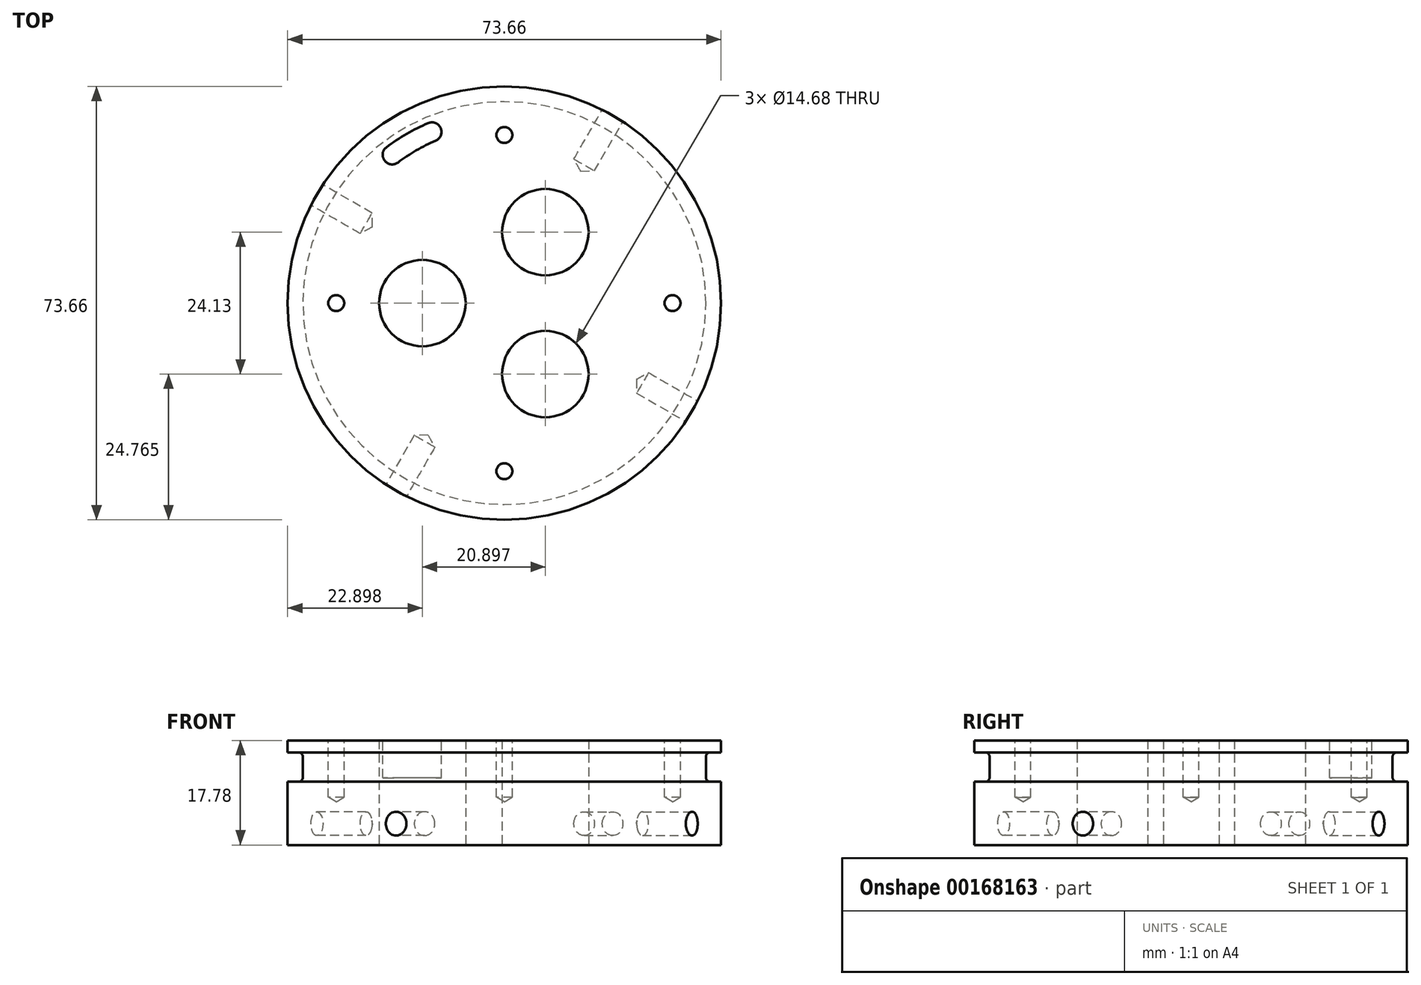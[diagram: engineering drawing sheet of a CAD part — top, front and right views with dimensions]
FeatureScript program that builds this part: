
annotation { "Feature Type Name" : "Feature", "Feature Type Description" : "" }
export const myFeature = defineFeature(function(context is Context, id is Id, definition is map)
    precondition{}
    {
        {
            var Q0;
            Q0=qCreatedBy(makeId("Top.planeOp"),FACE);
            var sketch = newSketch(context, id + "F0", { "sketchPlane" : qUnion([Q0])});
            skCircle(sketch, "E0", {"center": v(0, 0) * mm, "radius": 36.83 * mm});
            skSolve(sketch);
        }
        {
            var Q0;
            Q0=makeQuery(id+"F0.imprint","IMPRINT",FACE,{"disambiguationData":[TD([[makeQuery(id+"F0.imprint","IMPRINT",EDGE,{"derivedFrom":sQuery(id+"F0.wireOp",EDGE,"E0")}),1.0]])]});
            extrude(context, id + "F1", {"entities" : qUnion([Q0]), "depth" : 17.78 * mm});
        }
        {
            var Q0;
            {var subQ0=makeQuery(id+"FhJubWmbG7UBd7M_1.boolean.opBoolean","COPY",FACE,{"derivedFrom":makeQuery(id+"FhJubWmbG7UBd7M_1.opExtrude","SWEPT_FACE",FACE,{"disambiguationData":[OSD([sQuery(id+"FRuIeaWD6VeLny9_1.wireOp",EDGE,"idePJaX5-tPPE-BKw2-N1m4-zZUQrY6AHjir")])]})});Q0=makeQuery(id+"FOQC5dfjhO448EJ_1.boolean.opBoolean","SPLIT",FACE,{"disambiguationData":[TD([subQ0])],"derivedFrom":makeQuery(id+"FkcieFRIapZdHPD_1.boolean.opBoolean","SPLIT",FACE,{"disambiguationData":[TD([subQ0])],"derivedFrom":makeQuery(id+"F1.opExtrude","CAP_FACE",FACE,{"disambiguationData":[OSD([sQuery(id+"F0.wireOp",EDGE,"E0")])],"isStart":false})})});}
            var sketch = newSketch(context, id + "F2", { "sketchPlane" : qUnion([Q0])});
            skCircle(sketch, "E1", {"center": v(0, 0) * mm, "radius": 28.58 * mm, "construction": true});
            skLineSegment(sketch, "E2", {"start": v(0, 0) * mm, "end": v(28.57, 0) * mm, "construction": true});
            skPoint(sketch, "E3", {"position": v(28.58, 0) * mm});
            skPoint(sketch, "E4.1.0", {"position": v(0, 28.58) * mm});
            skPoint(sketch, "E4.2.0", {"position": v(-28.58, 0) * mm});
            skPoint(sketch, "E4.3.0", {"position": v(0, -28.58) * mm});
            skSolve(sketch);
        }
        {
            var Q0;
            Q0=sQuery(id+"F2.wireOp",VERTEX,"E3");
            var Q1;
            Q1=sQuery(id+"F2.wireOp",VERTEX,"E4.3.0");
            var Q2;
            Q2=sQuery(id+"F2.wireOp",VERTEX,"E4.2.0");
            var Q3;
            Q3=sQuery(id+"F2.wireOp",VERTEX,"E4.1.0");
            var Q4;
            Q4=makeQuery(id+"F1.opExtrude","SWEPT_BODY",BODY,{"disambiguationData":[OSD([sQuery(id+"F0.wireOp",EDGE,"E0")])]});
            hole(context, id + "F3", {"style" : HoleStyle.SIMPLE, "endStyle" : HoleEndStyle.BLIND, "standardTappedOrClearance" : lookupTablePath({ "standard" : "ANSI", "engagement" : "75%", "pitch" : "32 tpi", "size" : "#6", "type" : "Tapped" }), "standardBlindInLast" : lookupTablePath({ "standard" : "ANSI", "engagement" : "75%", "pitch" : "32 tpi", "size" : "#6", "type" : "Tapped" }), "holeDiameter" : 2.7 * mm, "holeDepth" : 9.65 * mm, "locations" : qUnion([Q0, Q1, Q2, Q3]), "scope" : qUnion([Q4]), "majorDiameter" : 3.5 * mm});
        }
        {
            var Q0;
            Q0=makeQuery(id+"FOQC5dfjhO448EJ_1.boolean.opBoolean","SPLIT",FACE,{"disambiguationData":[TD([makeQuery(id+"FhJubWmbG7UBd7M_1.boolean.opBoolean","COPY",FACE,{"derivedFrom":makeQuery(id+"FhJubWmbG7UBd7M_1.opExtrude","SWEPT_FACE",FACE,{"disambiguationData":[OSD([sQuery(id+"FRuIeaWD6VeLny9_1.wireOp",EDGE,"idePJaX5-tPPE-BKw2-N1m4-zZUQrY6AHjir")])]})})])],"derivedFrom":makeQuery(id+"F1.opExtrude","CAP_FACE",FACE,{"disambiguationData":[OSD([sQuery(id+"F0.wireOp",EDGE,"E0")])],"isStart":false})});
            cPlane(context, id + "F4", {"entities" : qUnion([Q0]), "cplaneType" : CPlaneType.OFFSET, "offset" : 2.03 * mm, "oppositeDirection" : true, "width" : 152.4 * mm, "height" : 152.4 * mm});
        }
        {
            var Q0;
            Q0=qCreatedBy(id+"F4.planeOp",FACE);
            var sketch = newSketch(context, id + "F5", { "sketchPlane" : qUnion([Q0])});
            skCircle(sketch, "E5", {"center": v(0, 0) * mm, "radius": 34.24 * mm});
            skCircle(sketch, "E6.0", {"center": v(0, 0) * mm, "radius": 36.83 * mm});
            skSolve(sketch);
        }
        {
            var Q0;
            Q0=qSketchRegion(id+"F5",true);
            extrude(context, id + "F6", {"entities" : qUnion([Q0]), "operationType" : NewBodyOperationType.REMOVE, "oppositeDirection" : true, "depth" : 5 * mm});
        }
        {
            var Q0;
            Q0=makeQuery(id+"F6.boolean.opBoolean","COPY",EDGE,{"derivedFrom":makeQuery(id+"F6.opExtrude","CAP_EDGE",EDGE,{"disambiguationData":[OSD([sQuery(id+"F5.wireOp",EDGE,"E5")])],"isStart":false})});
            var Q1;
            Q1=makeQuery(id+"F6.boolean.opBoolean","COPY",EDGE,{"derivedFrom":makeQuery(id+"F6.opExtrude","CAP_EDGE",EDGE,{"disambiguationData":[OSD([sQuery(id+"F5.wireOp",EDGE,"E5")])],"isStart":true})});
            fillet(context, id + "F7", {"entities" : qUnion([Q0, Q1]), "radius" : 0.76 * mm, "tangentPropagation" : true, "allowEdgeOverflow" : false});
        }
        {
            var Q0;
            {var subQ1=sQuery(id+"F0.wireOp",EDGE,"E0");var subQ2=makeQuery(id+"F1.opExtrude","SWEPT_FACE",FACE,{"disambiguationData":[OSD([subQ1])]});Q0=makeQuery(id+"FkcieFRIapZdHPD_1.boolean.opBoolean","SPLIT",FACE,{"disambiguationData":[TD([subQ2])],"derivedFrom":makeQuery(id+"F1.opExtrude","CAP_FACE",FACE,{"disambiguationData":[OSD([subQ1])],"isStart":false})});}
            var sketch = newSketch(context, id + "F8", { "sketchPlane" : qUnion([Q0])});
            skCircle(sketch, "E7.0", {"center": v(0, 0) * mm, "radius": 36.83 * mm, "construction": true});
            skPoint(sketch, "E8", {"position": v(-18.41, -31.9) * mm});
            skLineSegment(sketch, "E9", {"start": v(0, -36.83) * mm, "end": v(0, 0) * mm, "construction": true});
            skLineSegment(sketch, "E10", {"start": v(0, 0) * mm, "end": v(-17.96, -31.1) * mm, "construction": true});
            skLineSegment(sketch, "E11", {"start": v(-17.96, -31.1) * mm, "end": v(-18.41, -31.9) * mm, "construction": true});
            skLineSegment(sketch, "E12", {"start": v(0, 0) * mm, "end": v(18.41, 31.9) * mm, "construction": true});
            skLineSegment(sketch, "E13", {"start": v(18.41, 31.9) * mm, "end": v(0, 0) * mm, "construction": true});
            skLineSegment(sketch, "E14", {"start": v(31.9, -18.41) * mm, "end": v(0, 0) * mm, "construction": true});
            skLineSegment(sketch, "E15", {"start": v(0, 0) * mm, "end": v(-31.9, 18.41) * mm, "construction": true});
            skPoint(sketch, "E16", {"position": v(18.41, 31.9) * mm});
            skPoint(sketch, "E17", {"position": v(31.9, -18.41) * mm});
            skPoint(sketch, "E18", {"position": v(-31.9, 18.41) * mm});
            skSolve(sketch);
        }
        {
            var Q0;
            Q0=qCreatedBy(makeId("Front.planeOp"),FACE);
            var sketch = newSketch(context, id + "F9", { "sketchPlane" : qUnion([Q0])});
            skLineSegment(sketch, "E19", {"start": v(0, 0) * mm, "end": v(0, 38.57) * mm, "construction": true});
            skSolve(sketch);
        }
        {
            var Q0;
            Q0=sQuery(id+"F9.wireOp",EDGE,"E19");
            cPlane(context, id + "F10", {"entities" : qUnion([Q0]), "cplaneType" : CPlaneType.LINE_ANGLE, "offset" : 25.4 * mm, "angle" : 60 * degree, "width" : 152.4 * mm, "height" : 152.4 * mm});
        }
        {
            var Q0;
            Q0=sQuery(id+"F8.wireOp",VERTEX,"E8");
            var Q1;
            Q1=qCreatedBy(id+"F10.planeOp",FACE);
            cPlane(context, id + "F11", {"entities" : qUnion([Q0, Q1]), "cplaneType" : CPlaneType.PLANE_POINT, "offset" : 25.4 * mm, "width" : 152.4 * mm, "height" : 152.4 * mm});
        }
        {
            var Q0;
            Q0=qCreatedBy(id+"F11.planeOp",FACE);
            var Q1;
            Q1=sQuery(id+"F8.wireOp",VERTEX,"E16");
            cPlane(context, id + "F12", {"entities" : qUnion([Q0, Q1]), "cplaneType" : CPlaneType.PLANE_POINT, "offset" : 25.4 * mm, "width" : 152.4 * mm, "height" : 152.4 * mm});
        }
        {
            var Q0;
            Q0=sQuery(id+"F9.wireOp",EDGE,"E19");
            cPlane(context, id + "F13", {"entities" : qUnion([Q0]), "cplaneType" : CPlaneType.LINE_ANGLE, "offset" : 25.4 * mm, "angle" : 150 * degree, "width" : 152.4 * mm, "height" : 152.4 * mm});
        }
        {
            var Q0;
            Q0=sQuery(id+"F8.wireOp",VERTEX,"E18");
            var Q1;
            Q1=qCreatedBy(id+"F13.planeOp",FACE);
            cPlane(context, id + "F14", {"entities" : qUnion([Q0, Q1]), "cplaneType" : CPlaneType.PLANE_POINT, "offset" : 25.4 * mm, "width" : 152.4 * mm, "height" : 152.4 * mm});
        }
        {
            var Q0;
            Q0=qCreatedBy(id+"F13.planeOp",FACE);
            var Q1;
            Q1=sQuery(id+"F8.wireOp",VERTEX,"E17");
            cPlane(context, id + "F15", {"entities" : qUnion([Q0, Q1]), "cplaneType" : CPlaneType.PLANE_POINT, "offset" : 25.4 * mm, "width" : 152.4 * mm, "height" : 152.4 * mm});
        }
        {
            var Q0;
            Q0=qCreatedBy(id+"F11.planeOp",FACE);
            var sketch = newSketch(context, id + "F16", { "sketchPlane" : qUnion([Q0])});
            skLineSegment(sketch, "E20", {"start": v(0, 0) * mm, "end": v(0, 3.63) * mm, "construction": true});
            skPoint(sketch, "E21", {"position": v(0, 3.63) * mm});
            skSolve(sketch);
        }
        {
            var Q0;
            Q0=qCreatedBy(id+"F12.planeOp",FACE);
            var sketch = newSketch(context, id + "F17", { "sketchPlane" : qUnion([Q0])});
            skPoint(sketch, "E22", {"position": v(0, 3.63) * mm});
            skLineSegment(sketch, "E23.0", {"start": v(0, 0) * mm, "end": v(0, 3.63) * mm, "construction": true});
            skSolve(sketch);
        }
        {
            var Q0;
            Q0=qCreatedBy(id+"F14.planeOp",FACE);
            var sketch = newSketch(context, id + "F18", { "sketchPlane" : qUnion([Q0])});
            skLineSegment(sketch, "E24", {"start": v(0, 0) * mm, "end": v(0, 3.63) * mm, "construction": true});
            skLineSegment(sketch, "E25.0", {"start": v(-36.83, 0) * mm, "end": v(-36.83, 3.63) * mm, "construction": true});
            skPoint(sketch, "E26", {"position": v(0, 3.63) * mm});
            skLineSegment(sketch, "E27", {"start": v(-36.83, 3.63) * mm, "end": v(0, 3.63) * mm, "construction": true});
            skSolve(sketch);
        }
        {
            var Q0;
            Q0=qCreatedBy(id+"F15.planeOp",FACE);
            var sketch = newSketch(context, id + "F19", { "sketchPlane" : qUnion([Q0])});
            skLineSegment(sketch, "E28.0", {"start": v(0, 0) * mm, "end": v(0, 3.63) * mm, "construction": true});
            skPoint(sketch, "E29", {"position": v(0, 3.63) * mm});
            skSolve(sketch);
        }
        {
            var Q0;
            Q0=sQuery(id+"F19.wireOp",VERTEX,"E29");
            var Q1;
            Q1=makeQuery(id+"F1.opExtrude","SWEPT_BODY",BODY,{"disambiguationData":[OSD([sQuery(id+"F0.wireOp",EDGE,"E0")])]});
            hole(context, id + "F20", {"style" : HoleStyle.SIMPLE, "endStyle" : HoleEndStyle.BLIND, "oppositeDirection" : true, "standardTappedOrClearance" : lookupTablePath({ "standard" : "ANSI", "engagement" : "75%", "pitch" : "32 tpi", "size" : "#10", "type" : "Tapped" }), "standardBlindInLast" : lookupTablePath({ "standard" : "ANSI", "engagement" : "75%", "pitch" : "32 tpi", "size" : "#10", "type" : "Tapped" }), "holeDiameter" : 4.04 * mm, "holeDepth" : 9.65 * mm, "locations" : qUnion([Q0]), "scope" : qUnion([Q1]), "majorDiameter" : 4.83 * mm});
        }
        {
            var Q0;
            Q0=sQuery(id+"F18.wireOp",VERTEX,"E26");
            var Q1;
            Q1=makeQuery(id+"F1.opExtrude","SWEPT_BODY",BODY,{"disambiguationData":[OSD([sQuery(id+"F0.wireOp",EDGE,"E0")])]});
            hole(context, id + "F21", {"style" : HoleStyle.SIMPLE, "endStyle" : HoleEndStyle.BLIND, "standardTappedOrClearance" : lookupTablePath({ "standard" : "ANSI", "engagement" : "75%", "pitch" : "32 tpi", "size" : "#10", "type" : "Tapped" }), "standardBlindInLast" : lookupTablePath({ "standard" : "ANSI", "engagement" : "75%", "pitch" : "32 tpi", "size" : "#10", "type" : "Tapped" }), "holeDiameter" : 4.04 * mm, "holeDepth" : 9.65 * mm, "locations" : qUnion([Q0]), "scope" : qUnion([Q1]), "majorDiameter" : 4.83 * mm});
        }
        {
            var Q0;
            Q0=sQuery(id+"F16.wireOp",VERTEX,"E21");
            var Q1;
            Q1=makeQuery(id+"F1.opExtrude","SWEPT_BODY",BODY,{"disambiguationData":[OSD([sQuery(id+"F0.wireOp",EDGE,"E0")])]});
            hole(context, id + "F22", {"style" : HoleStyle.SIMPLE, "endStyle" : HoleEndStyle.BLIND, "oppositeDirection" : true, "standardTappedOrClearance" : lookupTablePath({ "standard" : "ANSI", "engagement" : "75%", "pitch" : "32 tpi", "size" : "#10", "type" : "Tapped" }), "standardBlindInLast" : lookupTablePath({ "standard" : "ANSI", "engagement" : "75%", "pitch" : "32 tpi", "size" : "#10", "type" : "Tapped" }), "holeDiameter" : 4.04 * mm, "holeDepth" : 9.65 * mm, "locations" : qUnion([Q0]), "scope" : qUnion([Q1]), "majorDiameter" : 4.83 * mm});
        }
        {
            var Q0;
            Q0=sQuery(id+"F17.wireOp",VERTEX,"E22");
            var Q1;
            Q1=makeQuery(id+"F1.opExtrude","SWEPT_BODY",BODY,{"disambiguationData":[OSD([sQuery(id+"F0.wireOp",EDGE,"E0")])]});
            hole(context, id + "F23", {"style" : HoleStyle.SIMPLE, "endStyle" : HoleEndStyle.BLIND, "standardTappedOrClearance" : lookupTablePath({ "standard" : "ANSI", "engagement" : "75%", "pitch" : "32 tpi", "size" : "#10", "type" : "Tapped" }), "standardBlindInLast" : lookupTablePath({ "standard" : "ANSI", "engagement" : "75%", "pitch" : "32 tpi", "size" : "#10", "type" : "Tapped" }), "holeDiameter" : 4.04 * mm, "holeDepth" : 9.65 * mm, "locations" : qUnion([Q0]), "scope" : qUnion([Q1]), "majorDiameter" : 4.83 * mm});
        }
        {
            var Q0;
            Q0=makeQuery(id+"F1.opExtrude","CAP_FACE",FACE,{"disambiguationData":[OSD([sQuery(id+"F0.wireOp",EDGE,"E0")])],"isStart":true});
            var sketch = newSketch(context, id + "F24", { "sketchPlane" : qUnion([Q0])});
            skPoint(sketch, "E30", {"position": v(-13.93, 0) * mm});
            skPoint(sketch, "E31.1.0", {"position": v(6.97, -12.07) * mm});
            skPoint(sketch, "E31.2.0", {"position": v(6.97, 12.07) * mm});
            skPoint(sketch, "E31.center", {"position": v(0, 0) * mm});
            skSolve(sketch);
        }
        {
            var Q0;
            Q0=sQuery(id+"F24.wireOp",VERTEX,"4a09c47b-9143-4afa-8474-e2cbf5050e91");
            var Q1;
            Q1=sQuery(id+"F24.wireOp",VERTEX,"E31.1.0");
            var Q2;
            Q2=sQuery(id+"F24.wireOp",VERTEX,"E30");
            var Q3;
            Q3=sQuery(id+"F24.wireOp",VERTEX,"E31.2.0");
            var Q4;
            Q4=makeQuery(id+"F1.opExtrude","SWEPT_BODY",BODY,{"disambiguationData":[OSD([sQuery(id+"F0.wireOp",EDGE,"E0")])]});
            hole(context, id + "F25", {"style" : HoleStyle.SIMPLE, "endStyle" : HoleEndStyle.THROUGH, "holeDiameter" : 14.68 * mm, "locations" : qUnion([Q0, Q1, Q2, Q3]), "scope" : qUnion([Q4]), "isTappedThrough" : true});
        }
        {
            var Q0;
            Q0=makeQuery(id+"F1.opExtrude","CAP_FACE",FACE,{"disambiguationData":[OSD([sQuery(id+"F0.wireOp",EDGE,"E0")])],"isStart":false});
            var sketch = newSketch(context, id + "F26", { "sketchPlane" : qUnion([Q0])});
            skCircle(sketch, "E32.0", {"center": v(0, 0) * mm, "radius": 34.24 * mm, "construction": true});
            skCircle(sketch, "E33", {"center": v(0, 0) * mm, "radius": 29.97 * mm, "construction": true});
            skCircle(sketch, "E34.0", {"center": v(0, 0) * mm, "radius": 33.22 * mm, "construction": true});
            skArc(sketch, "E35", {"start": v(-10.25, 28.16) * mm, "mid": v(-14.99, 25.96) * mm, "end": v(-19.27, 22.96) * mm});
            skLineSegment(sketch, "E36", {"start": v(-14.99, 25.96) * mm, "end": v(0, 0) * mm, "construction": true});
            skArc(sketch, "E37", {"start": v(-21.36, 25.45) * mm, "mid": v(-16.61, 28.77) * mm, "end": v(-11.36, 31.22) * mm});
            skLineSegment(sketch, "E38", {"start": v(-11.36, 31.22) * mm, "end": v(-10.25, 28.16) * mm});
            skLineSegment(sketch, "E39", {"start": v(-21.36, 25.45) * mm, "end": v(-19.27, 22.96) * mm});
            skLineSegment(sketch, "E40", {"start": v(0, 0) * mm, "end": v(-19.27, 22.96) * mm, "construction": true});
            skLineSegment(sketch, "E41", {"start": v(0, 0) * mm, "end": v(-10.25, 28.16) * mm, "construction": true});
            skSolve(sketch);
        }
        {
            var Q0;
            Q0 = qSketchRegion(id + "F26", true);
            extrude(context, id + "F27", {"entities" : qUnion([Q0]), "operationType" : NewBodyOperationType.REMOVE, "oppositeDirection" : true, "depth" : 6.35 * mm});
        }
        {
            var Q0;
            Q0=makeQuery(id+"F27.boolean.opBoolean","COPY",EDGE,{"derivedFrom":makeQuery(id+"F27.opExtrude","SWEPT_EDGE",EDGE,{"disambiguationData":[OSD([sQuery(id+"F26.wireOp",EDGE,"E37"),sQuery(id+"F26.wireOp",EDGE,"E38")])]})});
            var Q1;
            Q1=makeQuery(id+"F27.boolean.opBoolean","COPY",EDGE,{"derivedFrom":makeQuery(id+"F27.opExtrude","SWEPT_EDGE",EDGE,{"disambiguationData":[OSD([sQuery(id+"F26.wireOp",EDGE,"E37"),sQuery(id+"F26.wireOp",EDGE,"E39")])]})});
            var Q2;
            Q2=makeQuery(id+"F27.boolean.opBoolean","COPY",EDGE,{"derivedFrom":makeQuery(id+"F27.opExtrude","SWEPT_EDGE",EDGE,{"disambiguationData":[OSD([sQuery(id+"F26.wireOp",EDGE,"E35"),sQuery(id+"F26.wireOp",EDGE,"E39")])]})});
            var Q3;
            Q3=makeQuery(id+"F27.boolean.opBoolean","COPY",EDGE,{"derivedFrom":makeQuery(id+"F27.opExtrude","SWEPT_EDGE",EDGE,{"disambiguationData":[OSD([sQuery(id+"F26.wireOp",EDGE,"E35"),sQuery(id+"F26.wireOp",EDGE,"E38")])]})});
            fillet(context, id + "F28", {"entities" : qUnion([Q0, Q1, Q2, Q3]), "radius" : 1.59 * mm, "tangentPropagation" : true, "allowEdgeOverflow" : false});
        }
    });
